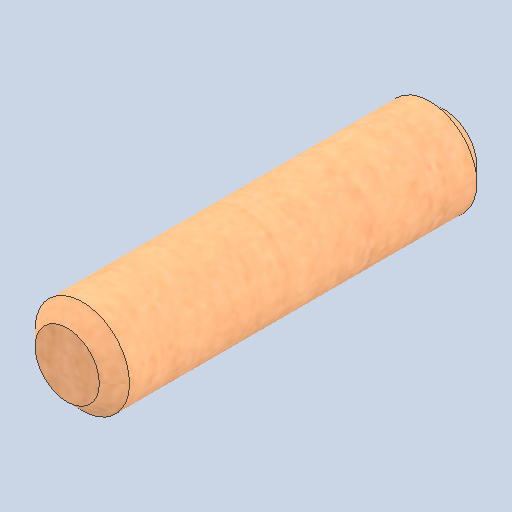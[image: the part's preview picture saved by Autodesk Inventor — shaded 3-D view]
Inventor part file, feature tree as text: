
AUTODESK INVENTOR PART (.ipt)
format: ipt  version: 2024 (Build 280153000, 153)  size: 173,568 bytes
history: native  units: in
note: dims shown in document units (in); Inventor stores cm internally (conversion verified against a paired STEP export)
features: extrude x1, chamfer x1, direct_edit x1, sketch x1, other x1
ambient origin geometry x8: Origin, YZ Plane, XZ Plane, XY Plane, X Axis, Y Axis, Z Axis, Center Point
bodies: Solid1 (feature_tree)
feature tree (5):
  extrude  "Extrusion1"  Depth=0.3937in TaperAngle=0.0deg
  chamfer  "Chamfer1"  Distance=0.015in Angle=45.0deg
  direct_edit  "Direct Edit1"
  sketch  "Sketch1"  dims[d0=0.0938in d1=0.375in d2=0.0in d3=0.015in d4=0.125in d5=45.0deg d6=3.937in d7=0.3937in d8=0.3937in]
  other  "Scale1"
